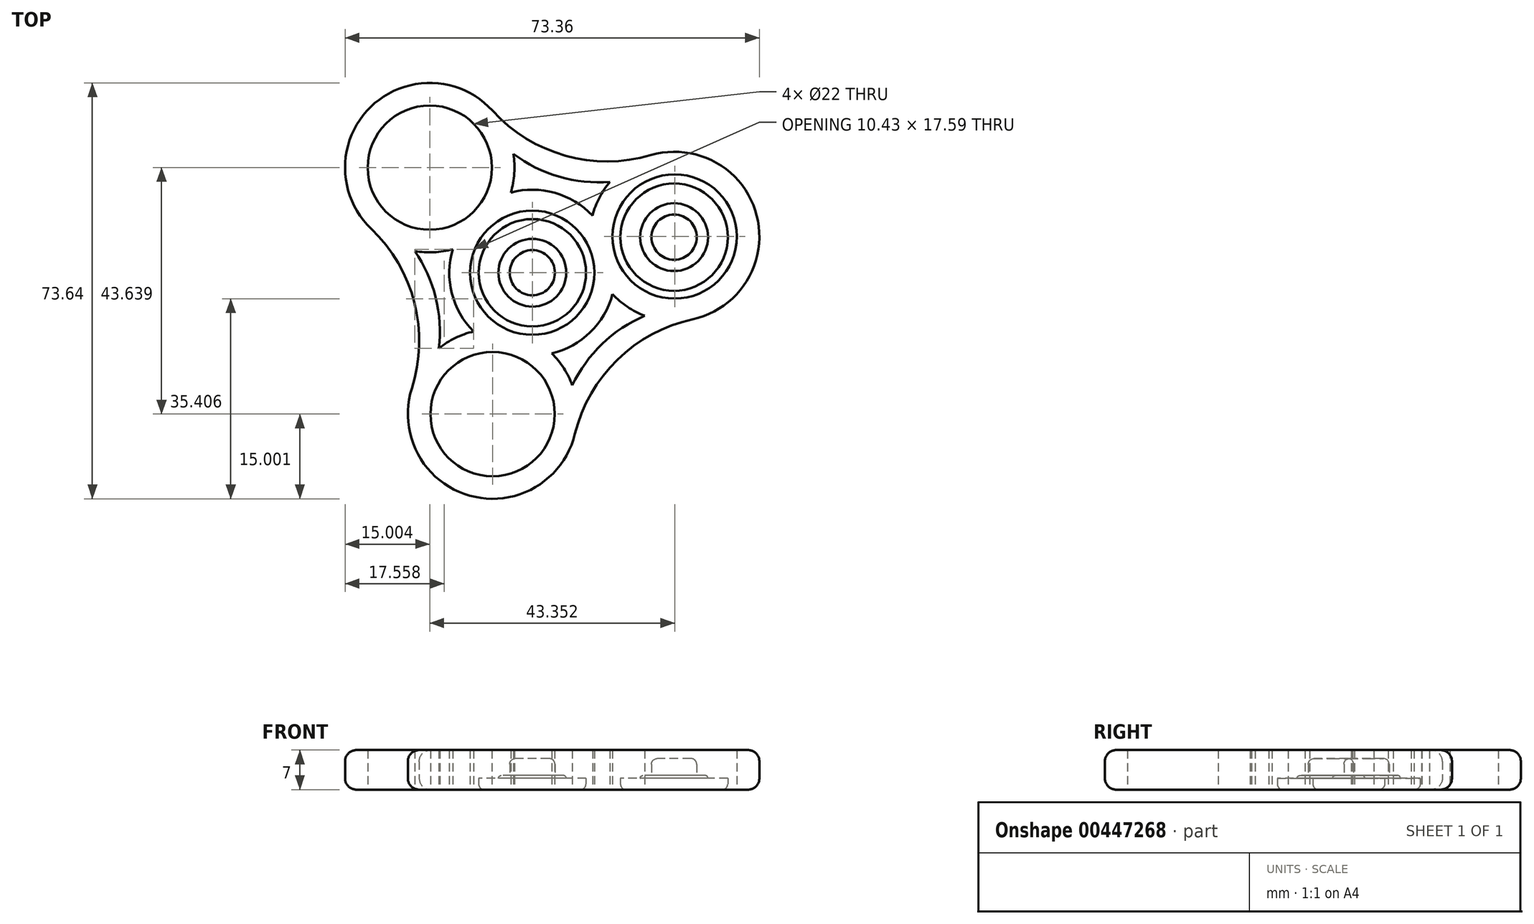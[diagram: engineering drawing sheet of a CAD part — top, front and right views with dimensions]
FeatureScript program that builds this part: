
annotation { "Feature Type Name" : "Feature", "Feature Type Description" : "" }
export const myFeature = defineFeature(function(context is Context, id is Id, definition is map)
    precondition{}
    {
        {
            var Q0;
            Q0=qCreatedBy(makeId("Top.planeOp"),FACE);
            var sketch = newSketch(context, id + "F0", { "sketchPlane" : qUnion([Q0])});
            skCircle(sketch, "E0", {"center": v(0, 0) * mm, "radius": 11 * mm});
            skArc(sketch, "E1", {"start": v(-3.82, 14.2) * mm, "mid": v(-3.2, 17.59) * mm, "end": v(-3.35, 21.03) * mm});
            skCircle(sketch, "E2.0", {"center": v(-18.16, 18.61) * mm, "radius": 11 * mm});
            skArc(sketch, "E3.1.1", {"start": v(-10.39, -10.4) * mm, "mid": v(-13.64, -11.56) * mm, "end": v(-16.53, -13.42) * mm});
            skCircle(sketch, "E3.1.2", {"center": v(-7.04, -25.03) * mm, "radius": 11 * mm});
            skArc(sketch, "E3.2.1", {"start": v(14.2, -3.8) * mm, "mid": v(16.83, -6.03) * mm, "end": v(19.89, -7.61) * mm});
            skCircle(sketch, "E3.2.2", {"center": v(25.2, 6.42) * mm, "radius": 11 * mm});
            skArc(sketch, "E4", {"start": v(-14.1, 4.17) * mm, "mid": v(-14.25, -3.63) * mm, "end": v(-10.39, -10.4) * mm});
            skArc(sketch, "E5.trimOffspring", {"start": v(10.66, 10.13) * mm, "mid": v(3.98, 14.16) * mm, "end": v(-3.82, 14.2) * mm});
            skArc(sketch, "E6.trimOffspring", {"start": v(3.44, -14.3) * mm, "mid": v(10.27, -10.53) * mm, "end": v(14.2, -3.8) * mm});
            skArc(sketch, "E7", {"start": v(-21.33, -20.47) * mm, "mid": v(-20.88, -5.32) * mm, "end": v(-28.52, 7.77) * mm});
            skArc(sketch, "E8", {"start": v(-16.53, -13.42) * mm, "mid": v(-17.1, -4.4) * mm, "end": v(-20.82, 3.85) * mm});
            skArc(sketch, "E9.1.1", {"start": v(19.89, -7.61) * mm, "mid": v(12.36, -12.61) * mm, "end": v(7.08, -19.95) * mm});
            skArc(sketch, "E9.1.2", {"start": v(28.4, -8.24) * mm, "mid": v(15.05, -15.42) * mm, "end": v(7.53, -28.59) * mm});
            skArc(sketch, "E9.2.1", {"start": v(-3.35, 21.03) * mm, "mid": v(4.75, 17) * mm, "end": v(13.74, 16.1) * mm});
            skArc(sketch, "E9.2.2", {"start": v(-7.06, 28.7) * mm, "mid": v(5.83, 20.74) * mm, "end": v(20.99, 20.82) * mm});
            skArc(sketch, "E10.trimOffspring", {"start": v(-20.82, 3.85) * mm, "mid": v(-17.44, 3.63) * mm, "end": v(-14.1, 4.17) * mm});
            skArc(sketch, "E11.trimOffspring", {"start": v(-21.33, -20.47) * mm, "mid": v(-11.1, -39.47) * mm, "end": v(7.53, -28.59) * mm});
            skArc(sketch, "E12.trimOffspring", {"start": v(7.08, -19.95) * mm, "mid": v(5.58, -16.92) * mm, "end": v(3.44, -14.3) * mm});
            skArc(sketch, "E13.trimOffspring", {"start": v(28.4, -8.24) * mm, "mid": v(39.73, 10.12) * mm, "end": v(20.99, 20.82) * mm});
            skArc(sketch, "E14.trimOffspring", {"start": v(13.74, 16.1) * mm, "mid": v(11.86, 13.3) * mm, "end": v(10.66, 10.13) * mm});
            skArc(sketch, "E15.trimOffspring", {"start": v(-7.06, 28.7) * mm, "mid": v(-28.63, 29.35) * mm, "end": v(-28.52, 7.77) * mm});
            skSolve(sketch);
        }
        {
            var Q0;
            Q0=makeQuery(id+"F0.imprint","IMPRINT",FACE,{"disambiguationData":[TD([[makeQuery(id+"F0.imprint","IMPRINT",EDGE,{"derivedFrom":sQuery(id+"F0.wireOp",EDGE,"E1")}),1.0]])]});
            extrude(context, id + "F1", {"entities" : qUnion([Q0]), "depth" : 7 * mm});
        }
        {
            var Q0;
            Q0=makeQuery(id+"F1.opExtrude","CAP_EDGE",EDGE,{"disambiguationData":[OSD([sQuery(id+"F0.wireOp",EDGE,"E11.trimOffspring")])],"isStart":false});
            fillet(context, id + "F2", {"entities" : qUnion([Q0]), "radius" : 2 * mm, "tangentPropagation" : true, "allowEdgeOverflow" : false});
        }
        {
            var Q0;
            Q0=makeQuery(id+"F1.opExtrude","CAP_EDGE",EDGE,{"disambiguationData":[OSD([sQuery(id+"F0.wireOp",EDGE,"E9.1.2")])],"isStart":true});
            fillet(context, id + "F3", {"entities" : qUnion([Q0]), "radius" : 2 * mm, "tangentPropagation" : true, "allowEdgeOverflow" : false});
        }
        {
            var Q0;
            Q0=qCreatedBy(makeId("Top.planeOp"),FACE);
            var sketch = newSketch(context, id + "F4", { "sketchPlane" : qUnion([Q0])});
            skCircle(sketch, "E16", {"center": v(0, 0) * mm, "radius": 9.5 * mm});
            skSolve(sketch);
        }
        {
            var Q0;
            Q0=makeQuery(id+"F4.imprint","IMPRINT",FACE,{"disambiguationData":[TD([[makeQuery(id+"F4.imprint","IMPRINT",EDGE,{"derivedFrom":sQuery(id+"F4.wireOp",EDGE,"E16")}),1.0]])]});
            extrude(context, id + "F5", {"entities" : qUnion([Q0]), "depth" : 2 * mm});
        }
        {
            var Q0;
            Q0=makeQuery(id+"F5.opExtrude","CAP_FACE",FACE,{"disambiguationData":[OSD([sQuery(id+"F4.wireOp",EDGE,"E16")])],"isStart":false});
            var sketch = newSketch(context, id + "F6", { "sketchPlane" : qUnion([Q0])});
            skCircle(sketch, "E17", {"center": v(0, 0) * mm, "radius": 6 * mm});
            skSolve(sketch);
        }
        {
            var Q0;
            Q0=makeQuery(id+"F6.imprint","IMPRINT",FACE,{"disambiguationData":[TD([[makeQuery(id+"F6.imprint","IMPRINT",EDGE,{"derivedFrom":sQuery(id+"F6.wireOp",EDGE,"E17")}),1.0]])]});
            extrude(context, id + "F7", {"entities" : qUnion([Q0]), "operationType" : NewBodyOperationType.ADD, "depth" : .5 * mm});
        }
        {
            var Q0;
            Q0=makeQuery(id+"F7.opExtrude","CAP_FACE",FACE,{"disambiguationData":[OSD([sQuery(id+"F6.wireOp",EDGE,"E17")])],"isStart":false});
            var sketch = newSketch(context, id + "F8", { "sketchPlane" : qUnion([Q0])});
            skCircle(sketch, "E18", {"center": v(0, 0) * mm, "radius": 4 * mm});
            skSolve(sketch);
        }
        {
            var Q0;
            Q0=makeQuery(id+"F8.imprint","IMPRINT",FACE,{"disambiguationData":[TD([[makeQuery(id+"F8.imprint","IMPRINT",EDGE,{"derivedFrom":sQuery(id+"F8.wireOp",EDGE,"E18")}),1.0]])]});
            extrude(context, id + "F9", {"entities" : qUnion([Q0]), "operationType" : NewBodyOperationType.ADD, "depth" : 3 * mm});
        }
        {
            var Q0;
            Q0=makeQuery(id+"F9.opExtrude","CAP_EDGE",EDGE,{"disambiguationData":[OSD([sQuery(id+"F8.wireOp",EDGE,"E18")])],"isStart":false});
            fillet(context, id + "F10", {"entities" : qUnion([Q0]), "radius" : 1 * mm, "tangentPropagation" : true, "allowEdgeOverflow" : false});
        }
        {
            var Q0;
            Q0=makeQuery(id+"F7.opExtrude","CAP_EDGE",EDGE,{"disambiguationData":[OSD([sQuery(id+"F6.wireOp",EDGE,"E17")])],"isStart":false});
            fillet(context, id + "F11", {"entities" : qUnion([Q0]), "radius" : .5 * mm, "tangentPropagation" : true, "allowEdgeOverflow" : false});
        }
        {
            var Q0;
            Q0=makeQuery(id+"F5.opExtrude","CAP_EDGE",EDGE,{"disambiguationData":[OSD([sQuery(id+"F4.wireOp",EDGE,"E16")])],"isStart":true});
            fillet(context, id + "F12", {"entities" : qUnion([Q0]), "radius" : 1 * mm, "tangentPropagation" : true, "allowEdgeOverflow" : false});
        }
        {
            var Q0;
            Q0=makeQuery(id+"F5.opExtrude","SWEPT_BODY",BODY,{"disambiguationData":[OSD([sQuery(id+"F4.wireOp",EDGE,"E16")])]});
            transform(context, id + "F13", {"entities" : qUnion([Q0]), "transformType" : TransformType.TRANSLATION_3D, "dx" : 25.1 * mm, "dy" : 6.3 * mm, "dz" : 0 * mm, "makeCopy" : true});
        }
    });
